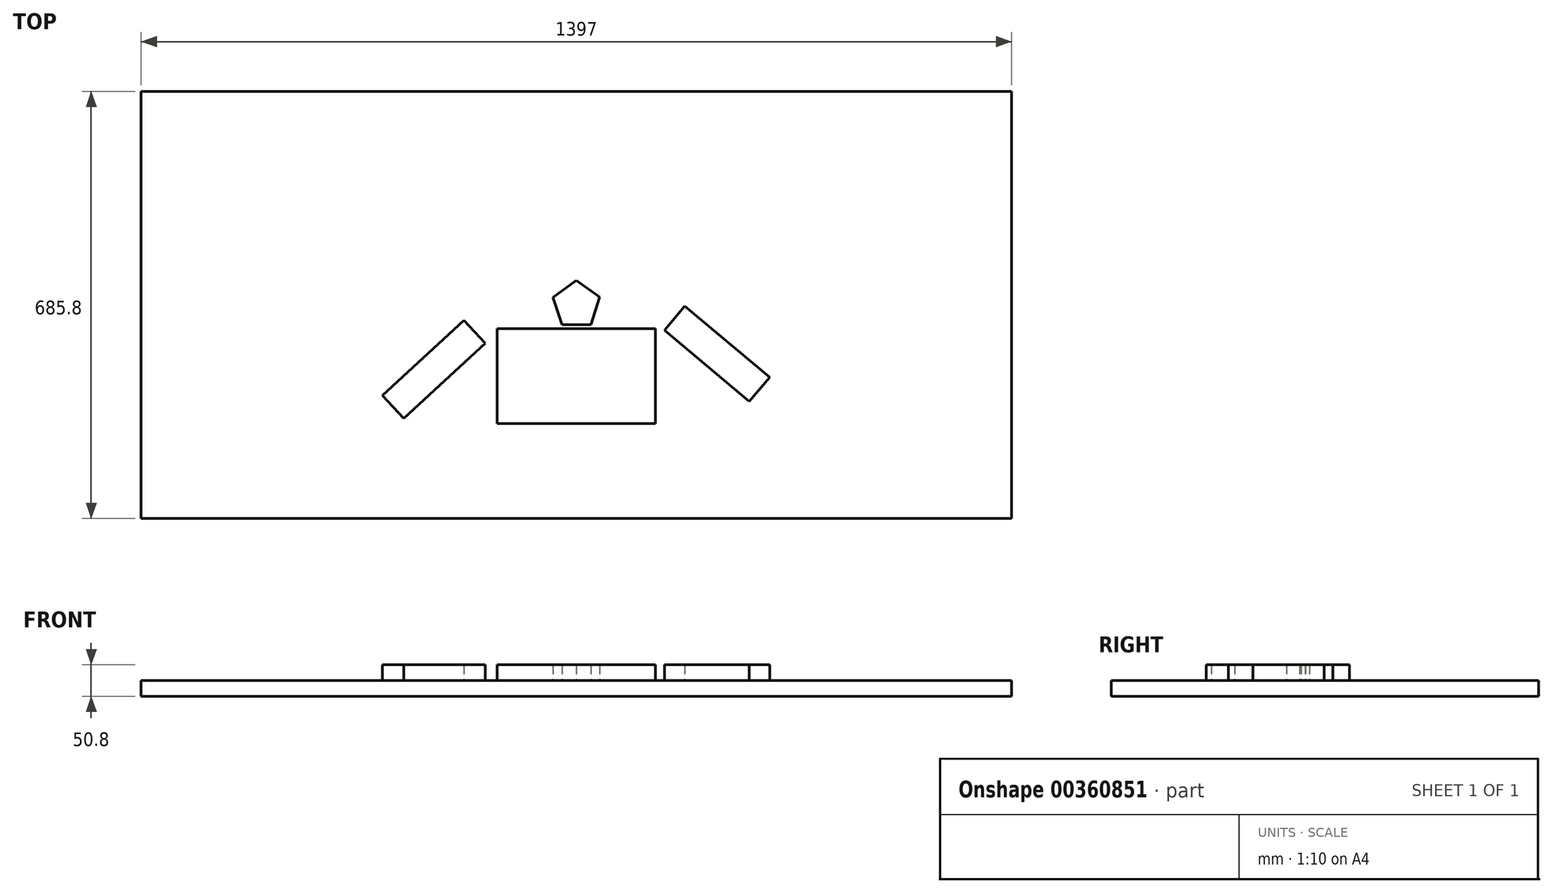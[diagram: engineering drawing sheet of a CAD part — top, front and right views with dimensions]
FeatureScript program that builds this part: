
annotation { "Feature Type Name" : "Feature", "Feature Type Description" : "" }
export const myFeature = defineFeature(function(context is Context, id is Id, definition is map)
    precondition{}
    {
        {
            var Q0;
            Q0=qCreatedBy(makeId("Top.planeOp"),FACE);
            var sketch = newSketch(context, id + "F0", { "sketchPlane" : qUnion([Q0])});
            skLineSegment(sketch, "E0.bottom", {"start": v(698.5, -342.9) * mm, "end": v(-698.5, -342.9) * mm});
            skLineSegment(sketch, "E0.top", {"start": v(698.5, 342.9) * mm, "end": v(-698.5, 342.9) * mm});
            skLineSegment(sketch, "E0.left", {"start": v(698.5, -342.9) * mm, "end": v(698.5, 342.9) * mm});
            skLineSegment(sketch, "E0.right", {"start": v(-698.5, -342.9) * mm, "end": v(-698.5, 342.9) * mm});
            skPoint(sketch, "E0.middle", {"position": v(0, 0) * mm});
            skSolve(sketch);
        }
        {
            var Q0;
            Q0 = qSketchRegion(id + "F0", true);
            extrude(context, id + "F1", {"entities" : qUnion([Q0]), "depth" : 25.4 * mm});
        }
        {
            var Q0;
            Q0=makeQuery(id+"F1.opExtrude","CAP_FACE",FACE,{"disambiguationData":[OSD([sQuery(id+"F0.wireOp",EDGE,"E0.bottom"),sQuery(id+"F0.wireOp",EDGE,"E0.top"),sQuery(id+"F0.wireOp",EDGE,"E0.left"),sQuery(id+"F0.wireOp",EDGE,"E0.right")])],"isStart":false});
            var sketch = newSketch(context, id + "F2", { "sketchPlane" : qUnion([Q0])});
            skLineSegment(sketch, "E1.bottom", {"start": v(127, -38.1) * mm, "end": v(-127, -38.1) * mm});
            skLineSegment(sketch, "E1.top", {"start": v(127, -190.5) * mm, "end": v(-127, -190.5) * mm});
            skLineSegment(sketch, "E1.left", {"start": v(127, -38.1) * mm, "end": v(127, -190.5) * mm});
            skLineSegment(sketch, "E1.right", {"start": v(-127, -38.1) * mm, "end": v(-127, -190.5) * mm});
            skPoint(sketch, "E1.middle", {"position": v(0, -114.3) * mm});
            skCircle(sketch, "E2.cCircle", {"center": v(0, 0) * mm, "radius": 31.75 * mm, "construction": true});
            skLineSegment(sketch, "E2.0", {"start": v(37.22, 12.46) * mm, "end": v(23.35, -31.55) * mm});
            skLineSegment(sketch, "E2.1", {"start": v(23.35, -31.55) * mm, "end": v(-22.79, -31.95) * mm});
            skLineSegment(sketch, "E2.2", {"start": v(-22.79, -31.95) * mm, "end": v(-37.43, 11.8) * mm});
            skLineSegment(sketch, "E2.3", {"start": v(-37.43, 11.8) * mm, "end": v(-0.35, 39.24) * mm});
            skLineSegment(sketch, "E2.4", {"start": v(-0.35, 39.24) * mm, "end": v(37.22, 12.46) * mm});
            skPoint(sketch, "E2.0.midPoint", {"position": v(30.28, -9.55) * mm});
            skLineSegment(sketch, "E3.bottom", {"start": v(-276.71, -182.54) * mm, "end": v(-311.16, -145.2) * mm});
            skLineSegment(sketch, "E3.top", {"start": v(-146.04, -61.97) * mm, "end": v(-180.49, -24.64) * mm});
            skLineSegment(sketch, "E3.left", {"start": v(-276.71, -182.54) * mm, "end": v(-146.04, -61.97) * mm});
            skLineSegment(sketch, "E3.right", {"start": v(-311.16, -145.2) * mm, "end": v(-180.49, -24.64) * mm});
            skPoint(sketch, "E3.middle", {"position": v(-228.6, -103.59) * mm});
            skLineSegment(sketch, "E4.bottom", {"start": v(310.17, -115.98) * mm, "end": v(277.52, -154.9) * mm});
            skLineSegment(sketch, "E4.top", {"start": v(173.97, -1.7) * mm, "end": v(141.32, -40.6) * mm});
            skLineSegment(sketch, "E4.left", {"start": v(310.17, -115.98) * mm, "end": v(173.97, -1.7) * mm});
            skLineSegment(sketch, "E4.right", {"start": v(277.52, -154.9) * mm, "end": v(141.32, -40.6) * mm});
            skPoint(sketch, "E4.middle", {"position": v(225.75, -78.3) * mm});
            skPoint(sketch, "E5", {"position": v(290.15, -165.5) * mm});
            skLineSegment(sketch, "E6.0", {"start": v(290.15, -165.5) * mm, "end": v(277.52, -154.9) * mm, "construction": true});
            skSolve(sketch);
        }
        {
            var Q0;
            Q0 = qSketchRegion(id + "F2", true);
            extrude(context, id + "F3", {"entities" : qUnion([Q0]), "depth" : 25.4 * mm});
        }
    });
